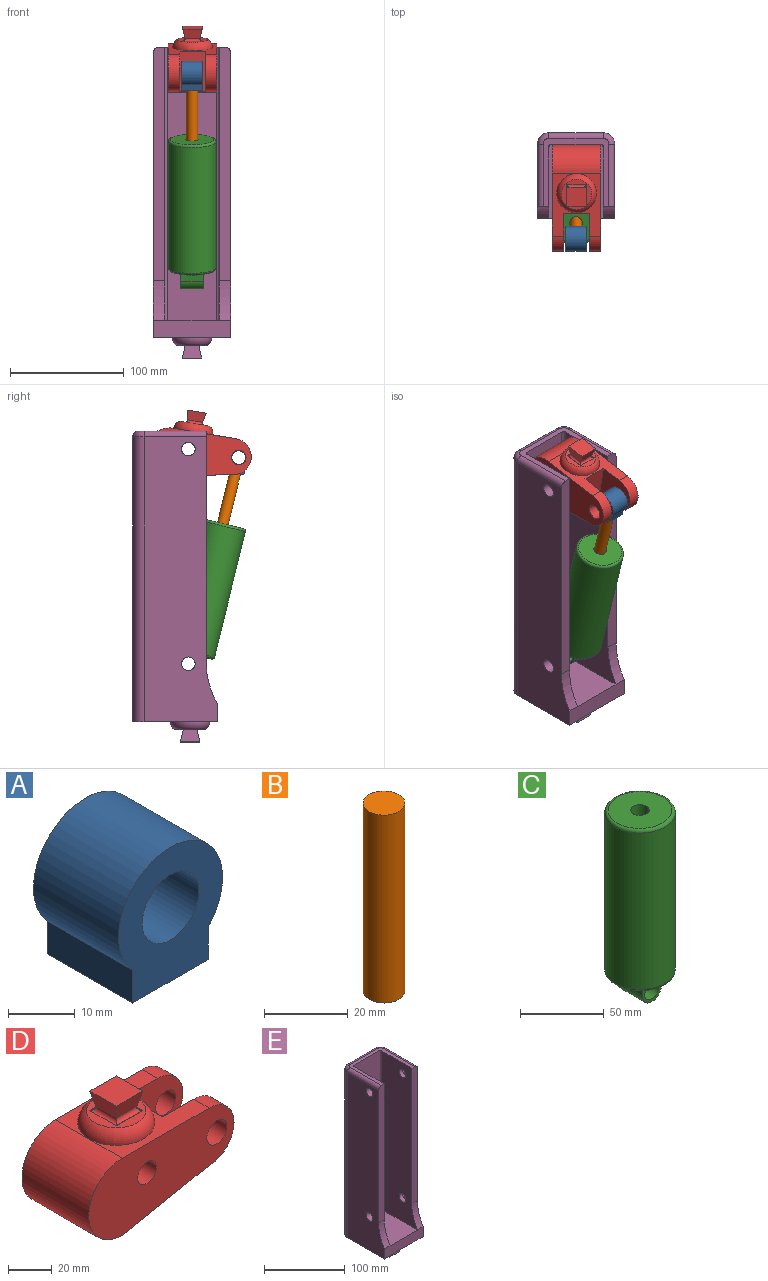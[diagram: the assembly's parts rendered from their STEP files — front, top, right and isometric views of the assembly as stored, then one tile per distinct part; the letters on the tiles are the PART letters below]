
ASSEMBLY  parts=5 mates=5
PART A: 7 faces, bbox 22x18x24.6 mm
  f0: cylinder r=11mm len=22mm, axis (0,1,0), area 921.6mm2, adj f1,f3,f5,f6
  f1: plane 18x6mm, normal (-1,0,0), area 108mm2, adj f0,f2,f5,f6
  f2: plane 18x16mm, normal (0,0,-1), area 288mm2, adj f1,f3,f5,f6
  f3: plane 18x6mm, normal (1,0,0), area 108mm2, adj f0,f2,f5,f6
  f4: cylinder r=6mm len=18mm, axis (0,1,0), area 678.6mm2, adj f5,f6
  f5: plane 24.55x22mm, normal (0,-1,0), area 324.9mm2, adj f0,f1,f2,f3,f4
  f6: plane 24.55x22mm, normal (0,1,0), area 324.9mm2, adj f0,f1,f2,f3,f4
PART B: 3 faces, bbox 10x10x55 mm
  f0: cylinder r=5mm len=55mm, axis (0,0,-1), area 1727.9mm2, adj f1,f2
  f1: plane 10x10mm, normal (0,0,1), area 78.5mm2, adj f0
  f2: plane 10x10mm, normal (0,0,-1), area 78.5mm2, adj f0
PART C: 13 faces, bbox 45.6x45.6x135 mm
  f0: cylinder r=21.05mm len=114.1mm, axis (0,0,-1), area 15091mm2, adj f3,f4
  f1: plane 38.1x38.1mm, normal (0,0,1), area 1045.1mm2, adj f4,f5
  f2: plane 38.1x38.1mm, normal (0,0,-1), area 820.1mm2, adj f3,f7,f8,f9,f10
  f3: torus R=19.05mm, axis (0,0,1), area 401.2mm2, adj f0,f2
  f4: torus R=19.05mm, axis (0,0,1), area 401.2mm2, adj f0,f1
  f5: cylinder r=5.5mm len=56.1mm, axis (0,0,1), area 1938.7mm2, adj f1,f6
  f6: plane 11x11mm, normal (0,0,1), area 95mm2, adj f5
  f7: plane 20x8.94mm, normal (-1,0,0), area 178.9mm2, adj f2,f9,f10,f11
  f8: plane 20x8.94mm, normal (1,0,0), area 178.9mm2, adj f2,f9,f10,f11
  f9: plane 16.94x16mm, normal (0,-1,0), area 130.5mm2, adj f2,f7,f8,f11,f12
  f10: plane 16.94x16mm, normal (0,1,0), area 130.5mm2, adj f2,f7,f8,f11,f12
  f11: cylinder r=8mm len=20mm, axis (0,1,0), area 502.7mm2, adj f7,f8,f9,f10
  f12: cylinder r=6mm len=20mm, axis (0,1,0), area 754mm2, adj f9,f10
PART D: 26 faces, bbox 93.5x43x60.9 mm
  f0: plane 16.93x8.44mm, normal (0.98,0,-0.22), area 130mm2, adj f19,f20,f21,f22,f23,f24
  f1: plane 16.93x8.44mm, normal (-0.98,0,-0.22), area 130mm2, adj f19,f20,f21,f22,f23,f25
  f2: plane 56x43mm, normal (0,0,1), area 985.9mm2, adj f4,f5,f8,f10,f11,f12,f13,f14
  f3: plane 56x43mm, normal (0.19,0,-0.98), area 1985.2mm2, adj f4,f5,f8,f10,f11,f12,f13,f14
  f4: cylinder r=16mm len=32mm, axis (0,1,0), area 502.7mm2, adj f2,f3,f10,f13
  f5: cylinder r=16mm len=32mm, axis (0,1,0), area 502.7mm2, adj f2,f3,f11,f14
  f6: cylinder r=6.46mm len=12.92mm, axis (0,1,0), area 405.7mm2, adj f10,f13
  f7: cylinder r=6.46mm len=12.92mm, axis (0,1,0), area 405.7mm2, adj f11,f14
  f8: cylinder r=21.5mm len=43mm, axis (0,1,0), area 2904.4mm2, adj f2,f3,f10,f11
  f9: cylinder r=6mm len=43mm, axis (0,1,0), area 1621.1mm2, adj f10,f11
  f10: plane 93.5x43mm, normal (0,-1,0), area 2984.1mm2, adj f2,f3,f4,f6,f8,f9
  f11: plane 93.5x43mm, normal (0,1,0), area 2984.1mm2, adj f2,f3,f5,f7,f8,f9
  f12: plane 35.93x23mm, normal (1,0,0), area 826.4mm2, adj f2,f3,f13,f14
  f13: plane 36x35.93mm, normal (0,1,0), area 950.4mm2, adj f2,f3,f4,f6,f12
  f14: plane 36x35.93mm, normal (0,-1,0), area 950.4mm2, adj f2,f3,f5,f7,f12
  f15: torus R=9.5mm, axis (0,0,-1), area 853.3mm2, adj f2,f16
  f16: plane 27x27mm, normal (0,0,1), area 282.5mm2, adj f15,f17,f18,f24,f25
  f17: plane 17.06x0.03mm, normal (0,-1,0), area 0.5mm2, adj f16,f23,f24,f25
  f18: plane 17.06x0.03mm, normal (0,1,0), area 0.5mm2, adj f16,f22,f24,f25
  f19: plane 17x16.93mm, normal (0,0,1), area 287.9mm2, adj f0,f1,f20,f21
  f20: plane 17x8.41mm, normal (0,0.98,-0.22), area 130.1mm2, adj f0,f1,f19,f22
  f21: plane 17x8.41mm, normal (0,-0.98,-0.22), area 130.1mm2, adj f0,f1,f19,f23
  f22: cylinder r=2mm len=16.37mm, axis (1,0,0), area 51mm2, adj f0,f1,f18,f20,f24,f25
  f23: cylinder r=2mm len=16.37mm, axis (-1,0,0), area 51mm2, adj f0,f1,f17,f21,f24,f25
  f24: cylinder r=2mm len=17mm, axis (0,-1,0), area 51.6mm2, adj f0,f16,f17,f18,f22,f23
  f25: cylinder r=2mm len=17mm, axis (0,1,0), area 51.6mm2, adj f1,f16,f17,f18,f22,f23
PART E: 54 faces, bbox 69.6x75.8x273.9 mm
  f0: plane 17x16.97mm, normal (0,0,-1), area 288.5mm2, adj f1,f2,f3,f52
  f1: plane 17x11mm, normal (0,0.98,0.22), area 163.6mm2, adj f0,f3,f4,f5,f48,f49,f50,f51
  f2: plane 17x11mm, normal (0,-0.98,0.22), area 163.6mm2, adj f0,f3,f4,f5,f48,f49,f50,f51
  f3: plane 17x0.02mm, normal (-1,0,0), area 0.4mm2, adj f0,f1,f2,f50
  f4: plane 12.06x0.13mm, normal (-1,0,0), area 1.5mm2, adj f1,f2,f5,f51
  f5: plane 27x27mm, normal (0,0,-1), area 368.5mm2, adj f1,f2,f4,f47,f48
  f6: plane 68x15.36mm, normal (0,-1,0), area 1027.1mm2, adj f8,f11,f15,f20,f22,f23,f45,f46
  f7: plane 205.9x10mm, normal (0,-1,0), area 2053.6mm2, adj f8,f15,f21,f29,f45
  f8: plane 251x65mm, normal (1,0,0), area 13540.2mm2, adj f6,f7,f17,f22,f29,f31,f32,f33
  f9: cylinder r=6mm len=12mm, axis (-1,0,0), area 226.2mm2, adj f15,f44
  f10: cylinder r=6mm len=12mm, axis (-1,0,0), area 226.2mm2, adj f15,f37
  f11: plane 241x62.5mm, normal (1,0,0), area 12541.9mm2, adj f6,f12,f16,f21,f23,f24,f30,f46
  f12: cylinder r=2.5mm len=241mm, axis (0,0,-1), area 946.4mm2, adj f11,f13,f21,f23
  f13: plane 241x43mm, normal (0,-1,0), area 10363mm2, adj f12,f14,f21,f23
  f14: cylinder r=2.5mm len=241mm, axis (0,0,-1), area 946.4mm2, adj f13,f15,f21,f23
  f15: plane 241x62.5mm, normal (-1,0,0), area 12541.9mm2, adj f6,f7,f9,f10,f14,f21,f23,f45
  f16: plane 205.9x10mm, normal (0,-1,0), area 2053.6mm2, adj f11,f20,f21,f25,f46
  f17: cylinder r=10mm len=251mm, axis (0,0,-1), area 3942.7mm2, adj f8,f18,f22,f28
  f18: plane 251x48mm, normal (0,1,0), area 12048mm2, adj f17,f19,f22,f27
  f19: cylinder r=10mm len=251mm, axis (0,0,-1), area 3942.7mm2, adj f18,f20,f22,f26
  f20: plane 251x65mm, normal (-1,0,0), area 13844.4mm2, adj f6,f16,f19,f22,f24,f25,f30,f46
  f21: plane 60x58mm, normal (0,0,1), area 832mm2, adj f7,f11,f12,f13,f14,f15,f16,f25
  f22: plane 75x68mm, normal (0,0,-1), area 4094.9mm2, adj f6,f8,f17,f18,f19,f20,f47
  f23: plane 65x48mm, normal (0,0,1), area 3117.3mm2, adj f6,f11,f12,f13,f14,f15
  f24: cylinder r=6mm len=12mm, axis (-1,0,0), area 377mm2, adj f11,f20
  f25: cylinder r=5mm len=55mm, axis (0,1,0), area 432mm2, adj f16,f20,f21,f26
  f26: torus R=5mm, axis (0,0,1), area 101mm2, adj f19,f21,f25,f27
  f27: cylinder r=5mm len=48mm, axis (1,0,0), area 377mm2, adj f18,f21,f26,f28
  f28: torus R=5mm, axis (0,0,1), area 101mm2, adj f17,f21,f27,f29
  f29: cylinder r=5mm len=55mm, axis (0,-1,0), area 432mm2, adj f7,f8,f21,f28
  f30: cylinder r=6mm len=12mm, axis (-1,0,0), area 377mm2, adj f11,f20
  f31: plane 8.71x5.12mm, normal (0,-0.86,0.51), area 40.4mm2, adj f8,f32,f36,f37
  f32: plane 8.79x4.98mm, normal (0,-0.87,-0.49), area 40.4mm2, adj f8,f31,f33,f37
  f33: plane 10.1x4mm, normal (0,-0.01,-1), area 40.4mm2, adj f8,f32,f34,f37
  f34: plane 8.71x5.12mm, normal (0,0.86,-0.51), area 40.4mm2, adj f8,f33,f35,f37
  f35: plane 8.79x4.98mm, normal (0,0.87,0.49), area 40.4mm2, adj f8,f34,f36,f37
  f36: plane 10.1x4mm, normal (0,0.01,1), area 40.4mm2, adj f8,f31,f35,f37
  f37: plane 20.21x17.58mm, normal (1,0,0), area 152.1mm2, adj f10,f31,f32,f33,f34,f35,f36
  f38: plane 8.75x5.06mm, normal (0,-0.87,0.5), area 40.4mm2, adj f8,f39,f43,f44
  f39: plane 8.75x5.05mm, normal (0,-0.87,-0.5), area 40.4mm2, adj f8,f38,f40,f44
  f40: plane 10.1x4mm, normal (0,0,-1), area 40.4mm2, adj f8,f39,f41,f44
  f41: plane 8.75x5.06mm, normal (0,0.87,-0.5), area 40.4mm2, adj f8,f40,f42,f44
  f42: plane 8.75x5.05mm, normal (0,0.87,0.5), area 40.4mm2, adj f8,f41,f43,f44
  f43: plane 10.1x4mm, normal (0,0,1), area 40.4mm2, adj f8,f38,f42,f44
  f44: plane 20.21x17.51mm, normal (1,0,0), area 152.1mm2, adj f9,f38,f39,f40,f41,f42,f43
  f45: cylinder r=65.36mm len=34.75mm, axis (-1,0,0), area 366.3mm2, adj f6,f7,f8,f15
  f46: cylinder r=65.36mm len=34.75mm, axis (-1,0,0), area 366.3mm2, adj f6,f11,f16,f20
  f47: torus R=9.5mm, axis (0,0,1), area 846.2mm2, adj f5,f22
  f48: plane 12.06x0.13mm, normal (1,0,0), area 1.5mm2, adj f1,f2,f5,f53
  f49: plane 16.99x10.85mm, normal (-0.98,0,0.22), area 161.6mm2, adj f1,f2,f50,f51
  f50: plane 16.99x0.04mm, normal (0,0,1), area 0.6mm2, adj f1,f2,f3,f49
  f51: plane 12.06x2.5mm, normal (0,0,-1), area 30.2mm2, adj f1,f2,f4,f49
  f52: plane 17x10.87mm, normal (0.98,0,0.22), area 162mm2, adj f0,f1,f2,f53
  f53: plane 12.06x2.5mm, normal (0,0,-1), area 30.1mm2, adj f1,f2,f48,f52
PLACE A rot(axis=(0.12,0.12,-0.99),90.8deg) t=(0,-4.79,75.29)mm
PLACE B rot(axis=(0.12,0.12,-0.99),90.8deg) t=(0,-30.84,-19.38)mm
PLACE C rot(axis=(0.12,0.12,-0.99),90.8deg) t=(0,-32.9,-10.95)mm
PLACE D rot(axis=(0.08,0.08,-0.99),90.4deg) t=(0.5,-63.65,87.93)mm
PLACE E at identity fixed
MATE revolute A.f0 <-> D.f6  axis (-1,0,0) through (-9,-61.14,104.57)mm
MATE slider B.f0 <-> C.f5  axis (0,0.24,-0.97) through (0,-44.86,37.98)mm
MATE fastened A.f2 <-> B.f0  axis (0,0.24,-0.97) through (0,-57.92,91.41)mm
MATE revolute D.f9 <-> E.f9  axis (1,0,0) through (22,-16.76,112)mm
MATE revolute C.f11 <-> E.f10  axis (-1,0,0) through (-10,-16.76,-77)mm
